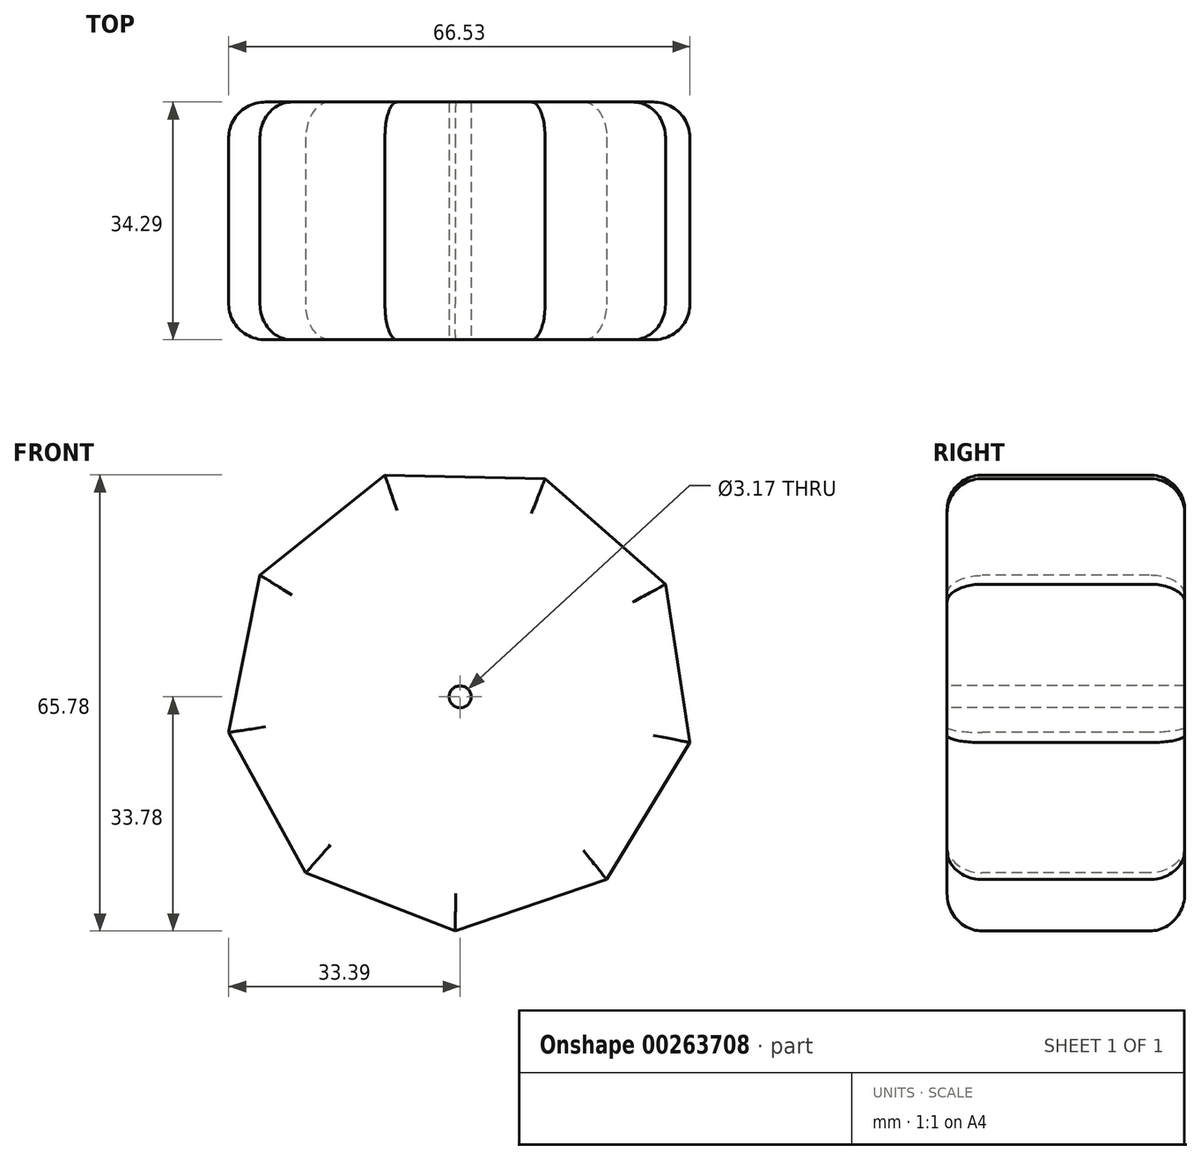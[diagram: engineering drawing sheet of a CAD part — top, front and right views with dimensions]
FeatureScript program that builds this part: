
annotation { "Feature Type Name" : "Feature", "Feature Type Description" : "" }
export const myFeature = defineFeature(function(context is Context, id is Id, definition is map)
    precondition{}
    {
        {
            var Q0;
            Q0=qCreatedBy(makeId("Front.planeOp"),FACE);
            var sketch = newSketch(context, id + "F0", { "sketchPlane" : qUnion([Q0])});
            skCircle(sketch, "E0.cCircle", {"center": v(0, 0) * mm, "radius": 31.75 * mm, "construction": true});
            skLineSegment(sketch, "E0.0", {"start": v(12.25, 31.49) * mm, "end": v(29.62, 16.25) * mm});
            skLineSegment(sketch, "E0.1", {"start": v(29.62, 16.25) * mm, "end": v(33.14, -6.6) * mm});
            skLineSegment(sketch, "E0.2", {"start": v(33.14, -6.6) * mm, "end": v(21.15, -26.35) * mm});
            skLineSegment(sketch, "E0.3", {"start": v(21.15, -26.35) * mm, "end": v(-0.74, -33.78) * mm});
            skLineSegment(sketch, "E0.4", {"start": v(-0.74, -33.78) * mm, "end": v(-22.28, -25.4) * mm});
            skLineSegment(sketch, "E0.5", {"start": v(-22.28, -25.4) * mm, "end": v(-33.4, -5.14) * mm});
            skLineSegment(sketch, "E0.6", {"start": v(-33.4, -5.14) * mm, "end": v(-28.88, 17.53) * mm});
            skLineSegment(sketch, "E0.7", {"start": v(-28.88, 17.53) * mm, "end": v(-10.86, 32) * mm});
            skLineSegment(sketch, "E0.8", {"start": v(-10.86, 32) * mm, "end": v(12.25, 31.49) * mm});
            skPoint(sketch, "E0.0.midPoint", {"position": v(20.94, 23.87) * mm});
            skCircle(sketch, "E1", {"center": v(0, 0) * mm, "radius": 1.59 * mm});
            skSolve(sketch);
        }
        {
            var Q0;
            Q0=makeQuery(id+"F0.imprint","IMPRINT",FACE,{"disambiguationData":[TD([[makeQuery(id+"F0.imprint","IMPRINT",EDGE,{"derivedFrom":sQuery(id+"F0.wireOp",EDGE,"E0.0")}),-1.0]])]});
            extrude(context, id + "F1", {"entities" : qUnion([Q0]), "oppositeDirection" : true, "depth" : 34.3 * mm});
        }
        {
            var Q0;
            Q0=makeQuery(id+"F1.opExtrude","CAP_EDGE",EDGE,{"disambiguationData":[OSD([sQuery(id+"F0.wireOp",EDGE,"E0.6")])],"isStart":true});
            var Q1;
            Q1=makeQuery(id+"F1.opExtrude","CAP_EDGE",EDGE,{"disambiguationData":[OSD([sQuery(id+"F0.wireOp",EDGE,"E0.5")])],"isStart":true});
            var Q2;
            Q2=makeQuery(id+"F1.opExtrude","CAP_EDGE",EDGE,{"disambiguationData":[OSD([sQuery(id+"F0.wireOp",EDGE,"E0.7")])],"isStart":true});
            var Q3;
            Q3=makeQuery(id+"F1.opExtrude","CAP_EDGE",EDGE,{"disambiguationData":[OSD([sQuery(id+"F0.wireOp",EDGE,"E0.8")])],"isStart":true});
            var Q4;
            Q4=makeQuery(id+"F1.opExtrude","CAP_EDGE",EDGE,{"disambiguationData":[OSD([sQuery(id+"F0.wireOp",EDGE,"E0.0")])],"isStart":true});
            var Q5;
            Q5=makeQuery(id+"F1.opExtrude","CAP_EDGE",EDGE,{"disambiguationData":[OSD([sQuery(id+"F0.wireOp",EDGE,"E0.1")])],"isStart":true});
            var Q6;
            Q6=makeQuery(id+"F1.opExtrude","CAP_EDGE",EDGE,{"disambiguationData":[OSD([sQuery(id+"F0.wireOp",EDGE,"E0.2")])],"isStart":true});
            var Q7;
            Q7=makeQuery(id+"F1.opExtrude","CAP_EDGE",EDGE,{"disambiguationData":[OSD([sQuery(id+"F0.wireOp",EDGE,"E0.3")])],"isStart":true});
            var Q8;
            Q8=makeQuery(id+"F1.opExtrude","CAP_EDGE",EDGE,{"disambiguationData":[OSD([sQuery(id+"F0.wireOp",EDGE,"E0.4")])],"isStart":true});
            var Q9;
            Q9=makeQuery(id+"F1.opExtrude","CAP_EDGE",EDGE,{"disambiguationData":[OSD([sQuery(id+"F0.wireOp",EDGE,"E0.2")])],"isStart":false});
            var Q10;
            Q10=makeQuery(id+"F1.opExtrude","CAP_EDGE",EDGE,{"disambiguationData":[OSD([sQuery(id+"F0.wireOp",EDGE,"E0.1")])],"isStart":false});
            var Q11;
            Q11=makeQuery(id+"F1.opExtrude","CAP_EDGE",EDGE,{"disambiguationData":[OSD([sQuery(id+"F0.wireOp",EDGE,"E0.0")])],"isStart":false});
            var Q12;
            Q12=makeQuery(id+"F1.opExtrude","CAP_EDGE",EDGE,{"disambiguationData":[OSD([sQuery(id+"F0.wireOp",EDGE,"E0.8")])],"isStart":false});
            var Q13;
            Q13=makeQuery(id+"F1.opExtrude","CAP_EDGE",EDGE,{"disambiguationData":[OSD([sQuery(id+"F0.wireOp",EDGE,"E0.7")])],"isStart":false});
            var Q14;
            Q14=makeQuery(id+"F1.opExtrude","CAP_EDGE",EDGE,{"disambiguationData":[OSD([sQuery(id+"F0.wireOp",EDGE,"E0.6")])],"isStart":false});
            var Q15;
            Q15=makeQuery(id+"F1.opExtrude","CAP_EDGE",EDGE,{"disambiguationData":[OSD([sQuery(id+"F0.wireOp",EDGE,"E0.5")])],"isStart":false});
            var Q16;
            Q16=makeQuery(id+"F1.opExtrude","CAP_EDGE",EDGE,{"disambiguationData":[OSD([sQuery(id+"F0.wireOp",EDGE,"E0.4")])],"isStart":false});
            var Q17;
            Q17=makeQuery(id+"F1.opExtrude","CAP_EDGE",EDGE,{"disambiguationData":[OSD([sQuery(id+"F0.wireOp",EDGE,"E0.3")])],"isStart":false});
            fillet(context, id + "F2", {"entities" : qUnion([Q0, Q1, Q2, Q3, Q4, Q5, Q6, Q7, Q8, Q9, Q10, Q11, Q12, Q13, Q14, Q15, Q16, Q17]), "radius" : 5.08 * mm, "tangentPropagation" : true, "allowEdgeOverflow" : false});
        }
    });
